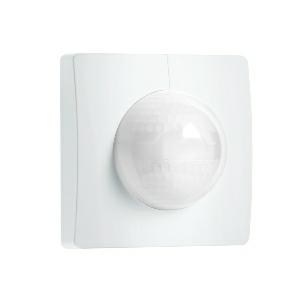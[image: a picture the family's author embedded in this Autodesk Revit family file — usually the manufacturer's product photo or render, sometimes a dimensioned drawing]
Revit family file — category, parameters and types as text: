
# Revit family: is_3180_057367
name_source: partatom
category: Elektroinstallationen
revit_build: Autodesk Revit 2016 (Build: 20190508_0715(x64)
units: mm (PartAtom-declared; Revit-internal decimal feet)

## family parameters
Basisbauteil = Fläche
Beim Laden mit Abzugskörper schneiden = Nein
Bemaßung runder Anschluss = Durchmesser verwenden
Beschriftungsausrichtung beibehalten = Nein
Gemeinsam genutzt = Nein
Raumberechnungspunkt = Nein
Teiletyp = Normal

## types (1)
- IS 3180
    Apparent Load = 0 VA
    Beschreibung = Type: Motion detectors; Dimensions (L x W x H): 78 x 94 x 94 mm; Mains power supply: 12 – 22,5 V / 50 – 60 Hz; Sensor Technology: passive infrared; Application, place: Indoors; Application, room: corridor / aisle, function room / ancillary room, stairwell, multi-storey / underground car park, outdoors, all round the building, courtyard & driveway, Indoors; Installation site: wall, corner; Installation: Concealed wiring; Switching zones: 448 switching zones; Electronic scalability: No; Mechanical scalability: No; Mounting height: 1,80 – 2,50 m; Optimum mounting height: 2 m; Detection angle: 180 °; Angle of aperture: 90 °; Sneak-by guard: Yes; Capability of masking out individual segments: Yes; Reach, radial: r = 4.5 m (32 m²); Reach, tangential: r = 20 m (628 m²); Twilight setting TEACH: Yes; Twilight setting: 2 – 1000 lx; Switching output 1, floating: No; Control output, Dali: Addressable/slave; Basic light level function: No; With bus coupling: Yes; Settings via: Bus; With remote control: No; Interconnection: Yes; IP-rating: IP20; Material: Plastic; Ambient temperature: -20 – 50 °C; Colour: white; Colour, RAL: 9003; Manufacturer's Warranty: 5 years; Version: DALI-2 IPD - concealed, sq.; PU1, EAN: 4007841057367
    Height = 94 mm  [stored 0.308399 ft]
    Hersteller = Steinel
    Length = 78 mm  [stored 0.255906 ft]
    Maximum range = 22.153 m
    ModVariant = Nein
    Modell = 057367
    Mounting Type = Recessed
    Number of Poles = 1
    OnlyDefault = Ja
    Power Factor = 1
    Product Name = IS 3180
    Product group = Sensor-switched indoor light
    ProductGroupID = 30
    Protection Class = Protection class
    Protection Degree = IP 20
    RlxData = <blob elided: 167801 chars, md5=baf9f3f0>
    Sensor characteristics = Semi circular 145°-300°
    Sensor type = Passive (infrared)
    SensorDataFile = <blob elided: 5082 chars, md5=d953030a>
    Type of entry = Motion
    Typenbild = produkt1_057367.jpg
    Typenkommentare = Product without accessories
    URL = http://relux.com
    VarID = ---
    Voltage = 0 V
    Vorgabe-Ansicht = 1800 mm
    Weight = 0.00 kg
    Width = 94 mm  [stored 0.308399 ft]

note: [stored X ft] marks values corroborated as IEEE doubles in the binary element streams (Revit-internal decimal feet)

## geometry (parser evidence)
native form markers: Sweep x18
no freeform markers — native parametric forms only
